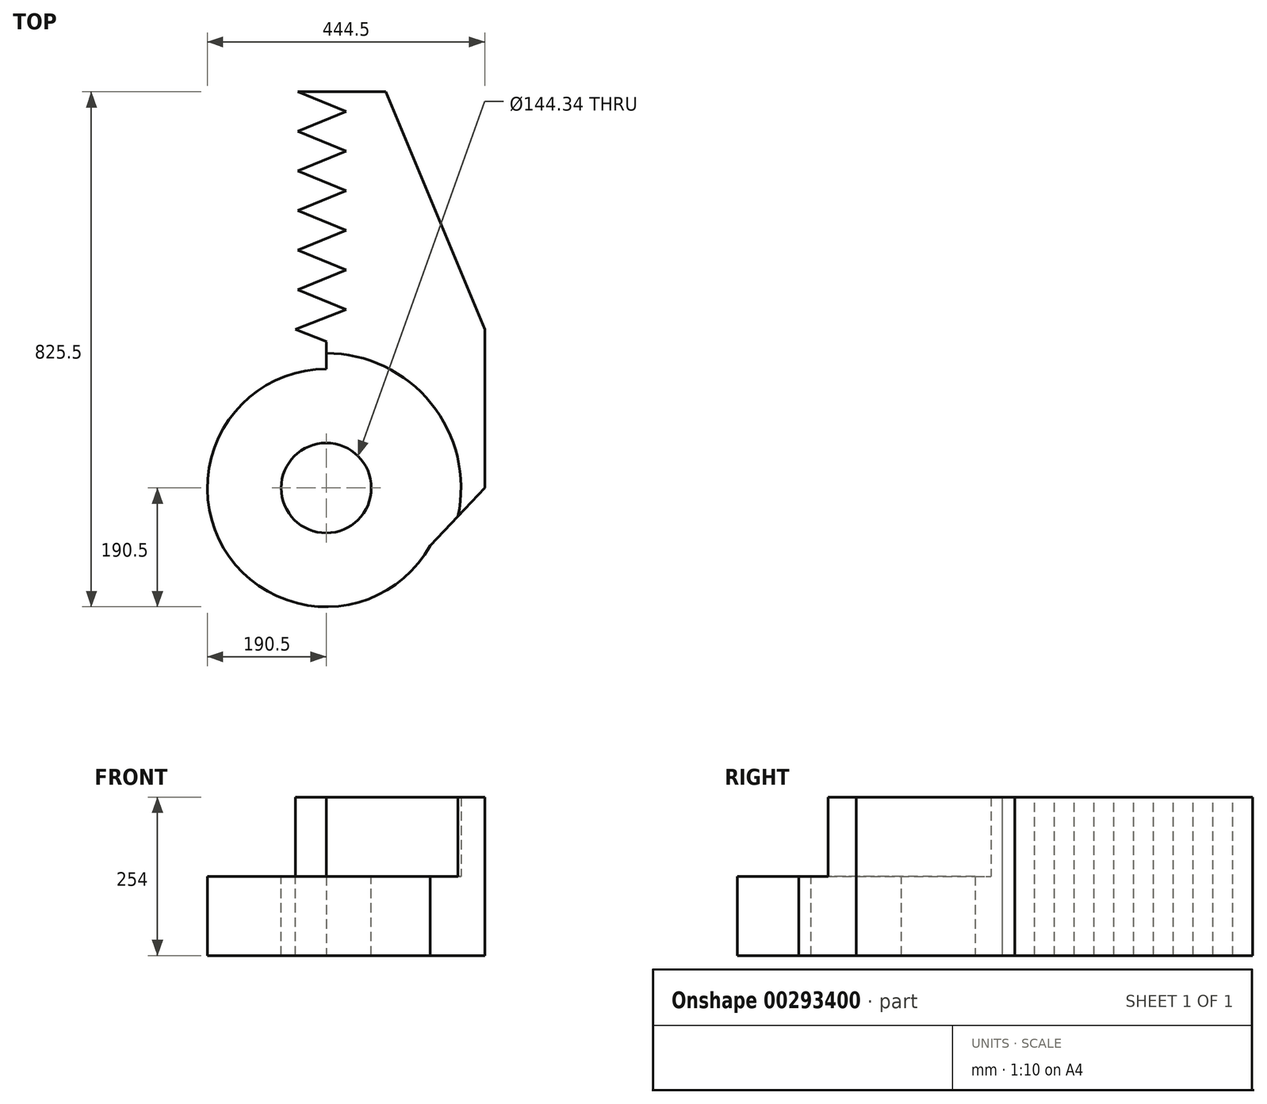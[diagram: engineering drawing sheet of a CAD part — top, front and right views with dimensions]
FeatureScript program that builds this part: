
annotation { "Feature Type Name" : "Feature", "Feature Type Description" : "" }
export const myFeature = defineFeature(function(context is Context, id is Id, definition is map)
    precondition{}
    {
        {
            var Q0;
            Q0=qCreatedBy(makeId("Top.planeOp"),FACE);
            var sketch = newSketch(context, id + "F0", { "sketchPlane" : qUnion([Q0])});
            skArc(sketch, "E0", {"start": v(0, 190.5) * mm, "mid": v(-164.1, -96.75) * mm, "end": v(166.69, -92.23) * mm});
            skLineSegment(sketch, "E1.bottom", {"start": v(0, 0) * mm, "end": v(254, 0) * mm});
            skLineSegment(sketch, "E1.left", {"start": v(0, 190.5) * mm, "end": v(0, 233.78) * mm});
            skLineSegment(sketch, "E1.right", {"start": v(254, 0) * mm, "end": v(254, 254) * mm});
            skLineSegment(sketch, "E2", {"start": v(254, 254) * mm, "end": v(95.25, 635) * mm});
            skLineSegment(sketch, "E3", {"start": v(95.25, 635) * mm, "end": v(31.75, 635) * mm});
            skLineSegment(sketch, "E4", {"start": v(31.75, 635) * mm, "end": v(31.75, 254) * mm});
            skLineSegment(sketch, "E5", {"start": v(31.75, 254) * mm, "end": v(0, 233.78) * mm});
            skLineSegment(sketch, "E6", {"start": v(254, 0) * mm, "end": v(166.69, -92.23) * mm});
            skSolve(sketch);
        }
        {
            var Q0;
            Q0=qSketchRegion(id+"F0",true);
            var Q1;
            Q1=qConstructionFilter(qBodyType(qCreatedBy(id+"F0",EDGE),BodyType.WIRE),ConstructionObject.NO);
            extrude(context, id + "F1", {"entities" : qUnion([Q0]), "surfaceEntities" : qUnion([Q1]), "depth" : 127 * mm});
        }
        {
            var Q0;
            Q0=makeQuery(id+"F1.opExtrude","CAP_FACE",FACE,{"disambiguationData":[OSD([sQuery(id+"F0.wireOp",EDGE,"E0"),sQuery(id+"F0.wireOp",EDGE,"E1.left"),sQuery(id+"F0.wireOp",EDGE,"E1.right"),sQuery(id+"F0.wireOp",EDGE,"E2"),sQuery(id+"F0.wireOp",EDGE,"E3"),sQuery(id+"F0.wireOp",EDGE,"E4"),sQuery(id+"F0.wireOp",EDGE,"E5"),sQuery(id+"F0.wireOp",EDGE,"E6")])],"isStart":false});
            var sketch = newSketch(context, id + "F2", { "sketchPlane" : qUnion([Q0])});
            skPoint(sketch, "E7.orphan", {"position": v(166.69, -92.23) * mm});
            skPoint(sketch, "E8.orphan", {"position": v(0, 190.5) * mm});
            skCircle(sketch, "E9", {"center": v(0, 0) * mm, "radius": 190.5 * mm, "construction": true});
            skArc(sketch, "E10.0", {"start": v(211.09, -45.33) * mm, "mid": v(167.93, 135.7) * mm, "end": v(0, 215.9) * mm});
            skLineSegment(sketch, "E11", {"start": v(0, 233.78) * mm, "end": v(0, 215.9) * mm});
            skLineSegment(sketch, "E12", {"start": v(254, 0) * mm, "end": v(211.09, -45.33) * mm});
            skLineSegment(sketch, "E13", {"start": v(254, 0) * mm, "end": v(254, 254) * mm});
            skLineSegment(sketch, "E14", {"start": v(254, 254) * mm, "end": v(95.25, 635) * mm});
            skLineSegment(sketch, "E15", {"start": v(95.25, 635) * mm, "end": v(31.75, 635) * mm});
            skLineSegment(sketch, "E16", {"start": v(31.75, 635) * mm, "end": v(31.75, 254) * mm});
            skLineSegment(sketch, "E17", {"start": v(31.75, 254) * mm, "end": v(0, 233.78) * mm});
            skSolve(sketch);
        }
        {
            var Q0;
            Q0=qSketchRegion(id+"F2",true);
            extrude(context, id + "F3", {"entities" : qUnion([Q0]), "operationType" : NewBodyOperationType.ADD, "depth" : 127 * mm});
        }
        {
            var Q0;
            Q0=makeQuery(id+"F1.opExtrude","CAP_FACE",FACE,{"disambiguationData":[OSD([sQuery(id+"F0.wireOp",EDGE,"E0"),sQuery(id+"F0.wireOp",EDGE,"E1.left"),sQuery(id+"F0.wireOp",EDGE,"E1.right"),sQuery(id+"F0.wireOp",EDGE,"E2"),sQuery(id+"F0.wireOp",EDGE,"E3"),sQuery(id+"F0.wireOp",EDGE,"E4"),sQuery(id+"F0.wireOp",EDGE,"E5"),sQuery(id+"F0.wireOp",EDGE,"E6")])],"isStart":false});
            var sketch = newSketch(context, id + "F4", { "sketchPlane" : qUnion([Q0])});
            skLineSegment(sketch, "E18", {"start": v(31.75, 603.25) * mm, "end": v(-45.77, 571.5) * mm});
            skLineSegment(sketch, "E19", {"start": v(-45.77, 571.5) * mm, "end": v(31.75, 539.75) * mm});
            skLineSegment(sketch, "E20", {"start": v(31.75, 539.75) * mm, "end": v(-45.77, 508) * mm});
            skLineSegment(sketch, "E21", {"start": v(-45.77, 508) * mm, "end": v(31.75, 476.25) * mm});
            skLineSegment(sketch, "E22", {"start": v(31.75, 476.25) * mm, "end": v(-45.77, 444.5) * mm});
            skLineSegment(sketch, "E23", {"start": v(-45.77, 444.5) * mm, "end": v(31.75, 412.75) * mm});
            skLineSegment(sketch, "E24", {"start": v(31.75, 412.75) * mm, "end": v(-45.77, 381) * mm});
            skLineSegment(sketch, "E25", {"start": v(-45.77, 381) * mm, "end": v(31.75, 349.25) * mm});
            skLineSegment(sketch, "E26", {"start": v(31.75, 349.25) * mm, "end": v(-45.77, 317.5) * mm});
            skLineSegment(sketch, "E27", {"start": v(-45.77, 317.5) * mm, "end": v(31.75, 285.75) * mm});
            skLineSegment(sketch, "E28", {"start": v(31.75, 285.75) * mm, "end": v(-49.62, 254) * mm});
            skLineSegment(sketch, "E29", {"start": v(31.75, 603.25) * mm, "end": v(31.75, 285.75) * mm});
            skLineSegment(sketch, "E30.0.1.1", {"start": v(-45.77, 635) * mm, "end": v(31.75, 603.25) * mm});
            skLineSegment(sketch, "E30.direction1", {"start": v(-45.77, 571.5) * mm, "end": v(126.95, 571.5) * mm, "construction": true});
            skLineSegment(sketch, "E30.direction2", {"start": v(-45.77, 571.5) * mm, "end": v(-45.77, 635) * mm, "construction": true});
            skLineSegment(sketch, "E31", {"start": v(31.75, 603.25) * mm, "end": v(31.75, 635) * mm});
            skLineSegment(sketch, "E32", {"start": v(31.75, 635) * mm, "end": v(-45.77, 635) * mm});
            skPoint(sketch, "E33.orphan", {"position": v(31.75, 222.25) * mm});
            skLineSegment(sketch, "E34", {"start": v(31.75, 285.75) * mm, "end": v(31.75, 254) * mm});
            skLineSegment(sketch, "E35", {"start": v(31.75, 254) * mm, "end": v(31.75, 222.25) * mm});
            skLineSegment(sketch, "E36", {"start": v(31.75, 222.25) * mm, "end": v(-49.62, 254) * mm});
            skSolve(sketch);
        }
        {
            var Q0;
            Q0=qSketchRegion(id+"F4",true);
            var Q1;
            Q1=makeQuery(id+"F1.opExtrude","CAP_FACE",FACE,{"disambiguationData":[OSD([sQuery(id+"F0.wireOp",EDGE,"E0"),sQuery(id+"F0.wireOp",EDGE,"E1.left"),sQuery(id+"F0.wireOp",EDGE,"E1.right"),sQuery(id+"F0.wireOp",EDGE,"E2"),sQuery(id+"F0.wireOp",EDGE,"E3"),sQuery(id+"F0.wireOp",EDGE,"E4"),sQuery(id+"F0.wireOp",EDGE,"E5"),sQuery(id+"F0.wireOp",EDGE,"E6")])],"isStart":true});
            extrude(context, id + "F5", {"entities" : qUnion([Q0]), "operationType" : NewBodyOperationType.ADD, "endBound" : BoundingType.UP_TO_SURFACE, "oppositeDirection" : true, "endBoundEntityFace" : qUnion([Q1]), "depth" : 25.4 * mm, "hasSecondDirection" : true, "secondDirectionOppositeDirection" : false, "secondDirectionDepth" : 127 * mm});
        }
        {
            var Q0;
            Q0=makeQuery(id+"F1.opExtrude","CAP_FACE",FACE,{"disambiguationData":[OSD([sQuery(id+"F0.wireOp",EDGE,"E0"),sQuery(id+"F0.wireOp",EDGE,"E1.left"),sQuery(id+"F0.wireOp",EDGE,"E1.right"),sQuery(id+"F0.wireOp",EDGE,"E2"),sQuery(id+"F0.wireOp",EDGE,"E3"),sQuery(id+"F0.wireOp",EDGE,"E4"),sQuery(id+"F0.wireOp",EDGE,"E5"),sQuery(id+"F0.wireOp",EDGE,"E6")])],"isStart":false});
            var sketch = newSketch(context, id + "F6", { "sketchPlane" : qUnion([Q0])});
            skCircle(sketch, "E37", {"center": v(0, 0) * mm, "radius": 72.17 * mm});
            skSolve(sketch);
        }
        {
            var Q0;
            Q0=qSketchRegion(id+"F6",true);
            extrude(context, id + "F7", {"entities" : qUnion([Q0]), "operationType" : NewBodyOperationType.REMOVE, "oppositeDirection" : true, "depth" : 266.7 * mm});
        }
    });
